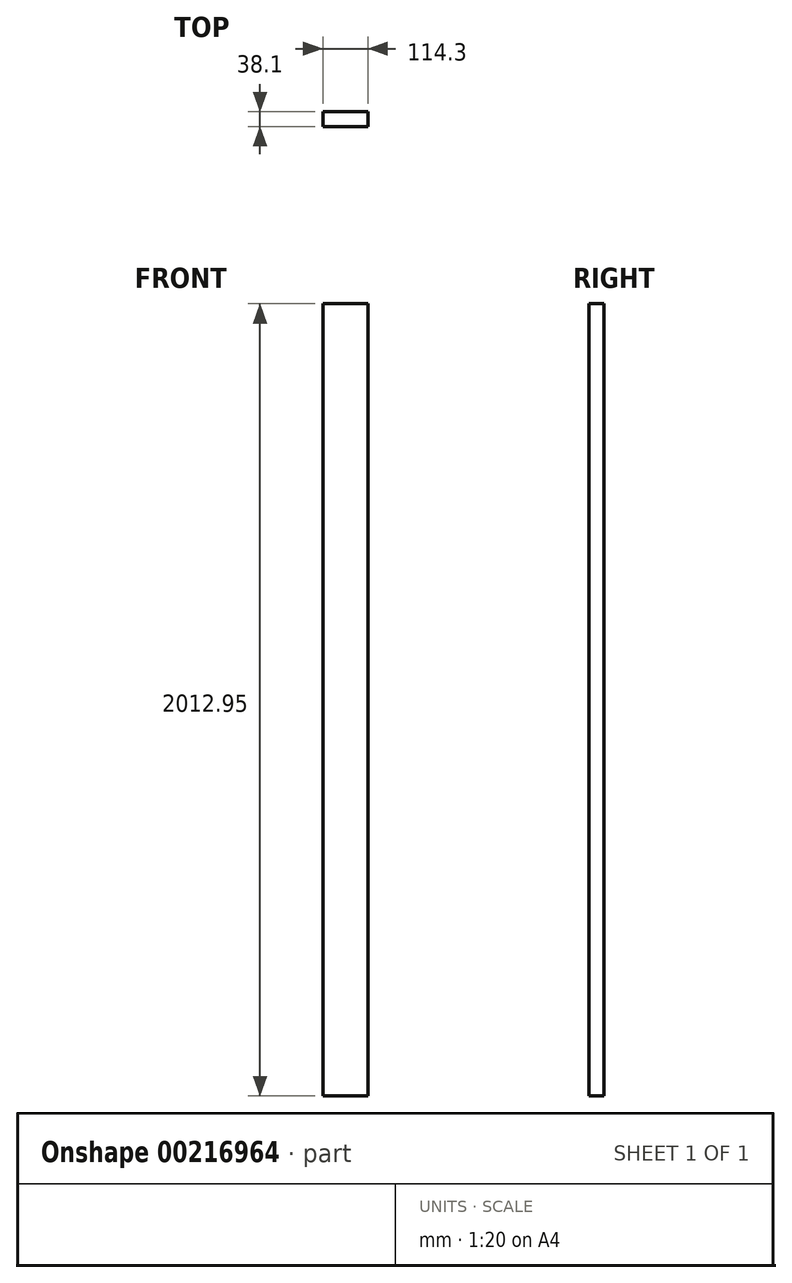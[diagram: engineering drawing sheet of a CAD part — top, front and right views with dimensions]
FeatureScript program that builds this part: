
annotation { "Feature Type Name" : "Feature", "Feature Type Description" : "" }
export const myFeature = defineFeature(function(context is Context, id is Id, definition is map)
    precondition{}
    {
        {
            var Q0;
            Q0=qCreatedBy(makeId("Front.planeOp"),FACE);
            var sketch = newSketch(context, id + "F0", { "sketchPlane" : qUnion([Q0])});
            skLineSegment(sketch, "E0.bottom", {"start": v(0, 0) * mm, "end": v(-114.3, 0) * mm});
            skLineSegment(sketch, "E0.top", {"start": v(0, 1828.8) * mm, "end": v(-114.3, 1828.8) * mm});
            skLineSegment(sketch, "E0.left", {"start": v(0, 0) * mm, "end": v(0, 1828.8) * mm});
            skLineSegment(sketch, "E0.right", {"start": v(-114.3, 0) * mm, "end": v(-114.3, 1828.8) * mm});
            skSolve(sketch);
        }
        {
            var Q0;
            Q0 = qSketchRegion(id + "F0", true);
            extrude(context, id + "F1", {"entities" : qUnion([Q0]), "depth" : 38.1 * mm, "offsetDistance" : 25.4 * mm});
        }
        {
            var Q0;
            Q0=makeQuery(id+"F1.opExtrude","SWEPT_FACE",FACE,{"disambiguationData":[OSD([sQuery(id+"F0.wireOp",EDGE,"E0.bottom")])]});
            extrude(context, id + "F2", {"entities" : qUnion([Q0]), "operationType" : NewBodyOperationType.ADD, "depth" : 184.15 * mm, "offsetDistance" : 25.4 * mm});
        }
    });
